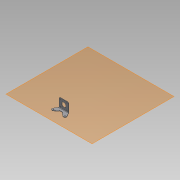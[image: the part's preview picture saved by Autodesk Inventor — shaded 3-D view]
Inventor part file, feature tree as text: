
AUTODESK INVENTOR PART (.ipt)
format: ipt  version: 2014 (Build 180170000, 170)  size: 174,592 bytes
history: native  units: mm
features: reference x7, sheet_metal_op x4, sketch x3, plane x2, fillet x2, other x2, extrude x1
ambient origin geometry x8: Origin, YZ Plane, XZ Plane, XY Plane, X Axis, Y Axis, Z Axis, Center Point
bodies: Solid1 (feature_tree)
feature tree (21):
  plane  "Work Plane1"
  sketch  "Sketch1"  dims[d0=14.0mm d1=14.0mm d2=30.0deg d3=30.0deg]
  plane  "Work Plane2"
  sheet_metal_op  "Face1"
  sheet_metal_op  "Flange1"
  extrude  "Extrusion2"  Depth=14.0mm
  fillet  "Fillet1"  [1 undecoded]
  fillet  "Fillet2"  [1 undecoded]
  reference  "Reference1"
  reference  "Reference2"
  other  "Plate1"
  sketch  "Sketch2"  dims[d4=1.0mm]
  other  "Plate2"
  sheet_metal_op  "Bend1"
  sheet_metal_op  "Corner1"
  sketch  "Sketch4"  dims[d5=1.0mm d6=2.0mm d7=2.0mm d8=1.0mm d9=4.0mm d10=2.0mm d11=45.0mm d12=90.0deg d13=2.0mm d14=8.0mm d15=2.0mm d16=2.0mm d20=22.0mm d21=2.0mm d22=0.0mm d23=6.0mm d24=3.0mm]
  reference  "Reference8"
  reference  "Reference9"
  reference  "Reference10"
  reference  "Reference11"
  reference  "Reference12"
note: 2 required parameter values undecoded (feature->parameter linkage not recoverable at this tier; creation-order binding heuristic only, values carry confidence <= 0.55)
